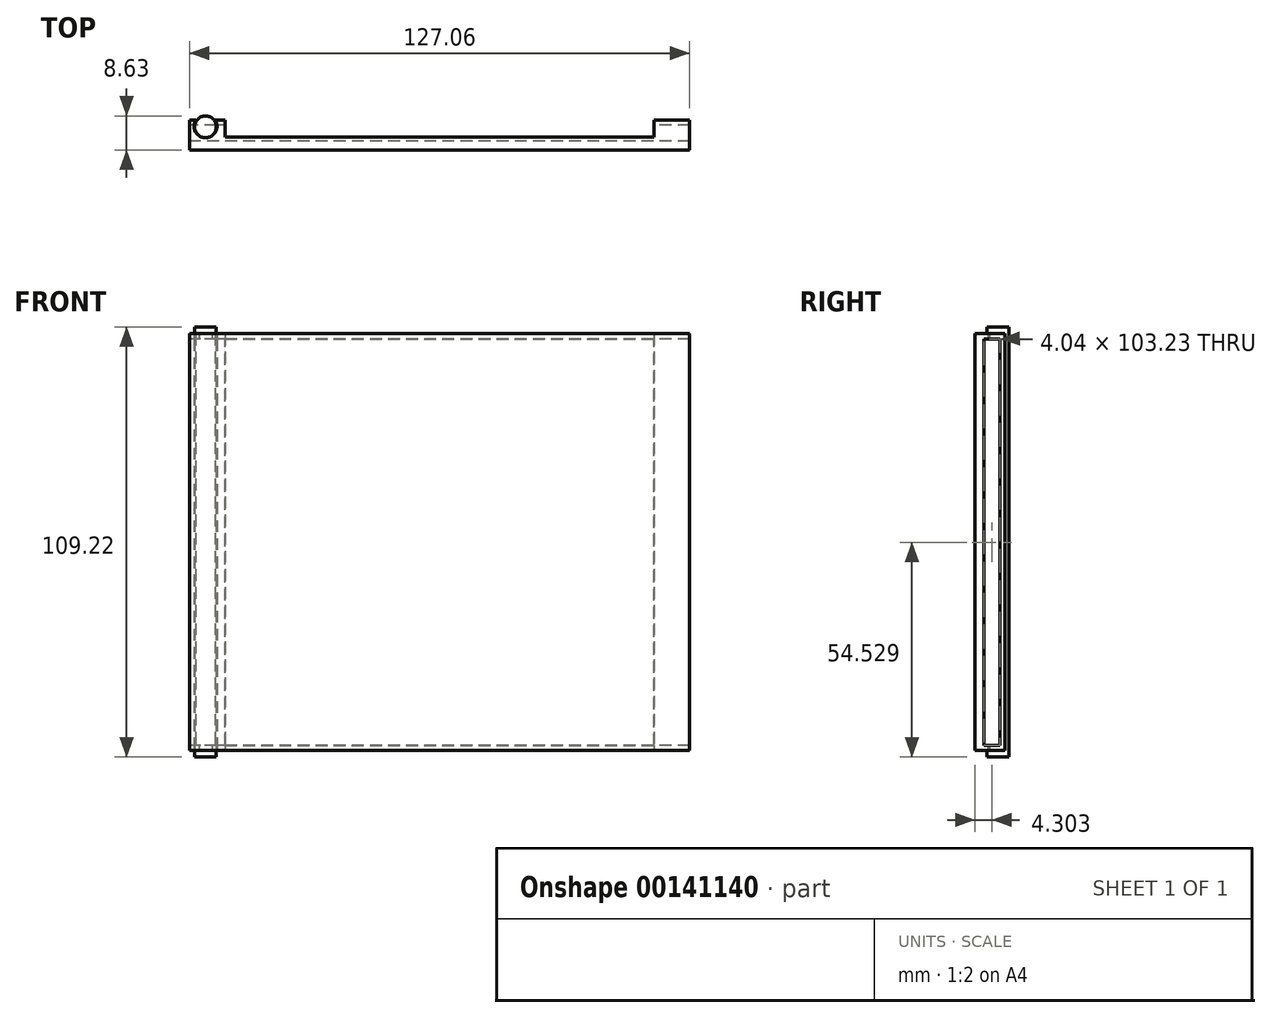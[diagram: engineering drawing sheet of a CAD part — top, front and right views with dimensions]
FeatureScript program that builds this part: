
annotation { "Feature Type Name" : "Feature", "Feature Type Description" : "" }
export const myFeature = defineFeature(function(context is Context, id is Id, definition is map)
    precondition{}
    {
        {
            var Q0;
            Q0=qCreatedBy(makeId("Front.planeOp"),FACE);
            var sketch = newSketch(context, id + "F0", { "sketchPlane" : qUnion([Q0])});
            skLineSegment(sketch, "E0.bottom", {"start": v(63.53, -52.94) * mm, "end": v(-63.53, -52.94) * mm});
            skLineSegment(sketch, "E0.top", {"start": v(63.53, 52.94) * mm, "end": v(-63.53, 52.94) * mm});
            skLineSegment(sketch, "E0.left", {"start": v(63.53, -52.94) * mm, "end": v(63.53, 52.94) * mm});
            skLineSegment(sketch, "E0.right", {"start": v(-63.53, -52.94) * mm, "end": v(-63.53, 52.94) * mm});
            skPoint(sketch, "E0.middle", {"position": v(0, 0) * mm});
            skSolve(sketch);
        }
        {
            var Q0;
            Q0 = qSketchRegion(id + "F0", true);
            extrude(context, id + "F1", {"entities" : qUnion([Q0]), "depth" : 7.62 * mm});
        }
        {
            var Q0;
            Q0=qCreatedBy(makeId("Front.planeOp"),FACE);
            var sketch = newSketch(context, id + "F2", { "sketchPlane" : qUnion([Q0])});
            skLineSegment(sketch, "E1.bottom", {"start": v(-54.5, 52.94) * mm, "end": v(54.5, 52.94) * mm});
            skLineSegment(sketch, "E1.top", {"start": v(-54.5, -52.94) * mm, "end": v(54.5, -52.94) * mm});
            skLineSegment(sketch, "E1.left", {"start": v(-54.5, 52.94) * mm, "end": v(-54.5, -52.94) * mm});
            skLineSegment(sketch, "E1.right", {"start": v(54.5, 52.94) * mm, "end": v(54.5, -52.94) * mm});
            skPoint(sketch, "E1.middle", {"position": v(0, 0) * mm});
            skSolve(sketch);
        }
        {
            var Q0;
            Q0=makeQuery(id+"F2.imprint","IMPRINT",FACE,{"disambiguationData":[TD([[makeQuery(id+"F2.imprint","IMPRINT",EDGE,{"derivedFrom":sQuery(id+"F2.wireOp",EDGE,"E1.bottom")}),-1.0]])]});
            extrude(context, id + "F3", {"entities" : qUnion([Q0]), "operationType" : NewBodyOperationType.REMOVE, "depth" : 4.32 * mm});
        }
        {
            var Q0;
            Q0=qCreatedBy(makeId("Top.planeOp"),FACE);
            var sketch = newSketch(context, id + "F4", { "sketchPlane" : qUnion([Q0])});
            skCircle(sketch, "E2", {"center": v(-59.48, -1.57) * mm, "radius": 2.91 * mm});
            skSolve(sketch);
        }
        {
            var Q0;
            Q0 = qSketchRegion(id + "F4", true);
            extrude(context, id + "F5", {"entities" : qUnion([Q0]), "operationType" : NewBodyOperationType.REMOVE, "depth" : 62.1 * mm, "hasSecondDirection" : true, "secondDirectionOppositeDirection" : true, "secondDirectionDepth" : 60.44 * mm});
        }
        {
            var Q0;
            Q0=qCreatedBy(makeId("Top.planeOp"),FACE);
            var sketch = newSketch(context, id + "F6", { "sketchPlane" : qUnion([Q0])});
            skCircle(sketch, "E3", {"center": v(-59.48, -1.75) * mm, "radius": 2.76 * mm});
            skSolve(sketch);
        }
        {
            var Q0;
            Q0 = qSketchRegion(id + "F6", true);
            extrude(context, id + "F7", {"entities" : qUnion([Q0]), "operationType" : NewBodyOperationType.ADD, "depth" : 54.6 * mm, "hasSecondDirection" : true, "secondDirectionOppositeDirection" : true, "secondDirectionDepth" : 54.6 * mm});
        }
        {
            var Q0;
            Q0=qCreatedBy(makeId("Right.planeOp"),FACE);
            var sketch = newSketch(context, id + "F8", { "sketchPlane" : qUnion([Q0])});
            skLineSegment(sketch, "E4.bottom", {"start": v(-1.3, 51.53) * mm, "end": v(-5.34, 51.53) * mm});
            skLineSegment(sketch, "E4.top", {"start": v(-1.3, -51.7) * mm, "end": v(-5.34, -51.7) * mm});
            skLineSegment(sketch, "E4.left", {"start": v(-1.3, 51.53) * mm, "end": v(-1.3, -51.7) * mm});
            skLineSegment(sketch, "E4.right", {"start": v(-5.34, 51.53) * mm, "end": v(-5.34, -51.7) * mm});
            skSolve(sketch);
        }
        {
            var Q0;
            Q0 = qSketchRegion(id + "F8", true);
            extrude(context, id + "F9", {"entities" : qUnion([Q0]), "operationType" : NewBodyOperationType.REMOVE, "depth" : 79 * mm, "hasSecondDirection" : true, "secondDirectionOppositeDirection" : true, "secondDirectionDepth" : 74.9 * mm});
        }
        {
            var Q0;
            Q0=qCreatedBy(makeId("Right.planeOp"),FACE);
            var sketch = newSketch(context, id + "F10", { "sketchPlane" : qUnion([Q0])});
            skLineSegment(sketch, "E5.bottom", {"start": v(-3.31, 51.47) * mm, "end": v(-4.6, 51.47) * mm});
            skLineSegment(sketch, "E5.top", {"start": v(-3.31, -50.55) * mm, "end": v(-4.6, -50.55) * mm});
            skLineSegment(sketch, "E5.left", {"start": v(-3.31, 51.47) * mm, "end": v(-3.31, -50.55) * mm});
            skLineSegment(sketch, "E5.right", {"start": v(-4.6, 51.47) * mm, "end": v(-4.6, -50.55) * mm});
            skSolve(sketch);
        }
        {
            var Q0;
            Q0 = qSketchRegion(id + "F10", true);
            extrude(context, id + "F11", {"entities" : qUnion([Q0]), "operationType" : NewBodyOperationType.REMOVE, "depth" : 76.04 * mm, "hasSecondDirection" : true, "secondDirectionOppositeDirection" : true, "secondDirectionDepth" : 72.7 * mm});
        }
    });
